# Revit family: ToothbrushHolder-Vitra-EternitySeries-A4487257
name_source: partatom
category: Plumbing Fixtures
revit_build: Autodesk Revit 2017 (Build: 20160225_1515(x64)
units: mm (PartAtom-declared; Revit-internal decimal feet)

## family parameters
Cut with Voids When Loaded = No
Host = Face
OmniClass Number = 23.45.05.14.99
OmniClass Title = Other Sanitary Washing Plumbing Fixtures
Part Type = Normal
Room Calculation Point = No
Round Connector Dimension = Use Diameter
Shared = Yes

## types (8) — shared parameters
BIMobject category = Sanitary - Accessories
CW Connection = No
Depth(mm) = 118 mm
Description = Eternity Toothbrush Holder
Design country = Turkey
HW Connection = No
Height(mm) = 103 mm  [stored 0.337927 ft]
IFC Classification = Sanitary Terminal
Manufacturer = Vitra
Manufacturer name = Vitra
Masterformat 2014 Code = 10 28 16
Masterformat 2014 Description = Bath Accessories
MountingType = Wall-mounted
NBS Referans Code = 35-75-89
NBS Referans Description = Toothbrush Holders
Nominal height = 0.000
Nominal width = 0.000
OmniClass Code = 23-31 25 00
OmniClass Description = Toilet and Bath Specialties
Product Type = Built-in Toothbrush Holder
Product certification = https://vitraglobal.com
Product data url = https://www.vitraglobal.com
Product family = EternitySeries
Product group = Toothbrush Holder
Technical description = https://www.vitra.com.tr
UNSPSC Code = 56
UNSPSC Description = Furniture and Furnishings
URL = https://vitraglobal.com
Uniclass 1.4 Code = L824
Uniclass 1.4 Description = Bathroom, toilet furniture and fittings
Uniclass 2.0 Code = PR-35-75-89
Uniclass 2.0 Description = Toothbrush Holders
Uniclass 2015 Code = Pr_40_20_76_89
Uniclass 2015 Name = Toothbrush holders
Uniformat II Code = E1090
Uniformat II Description = Other Equipment
Vent Connection = No
Warranty Period (Year) = 5 Years
Waste Connection = No
Weight Net (kg) = 0,620
Width(mm) = 103 mm  [stored 0.337927 ft]
Youtube = https://www.youtube.com
zero-valued in all types: CWFU, Cost, Default Elevation, HWFU, WFU

## per-type parameters (varying)
| type | Article No. (default) | Coating Material | Color | Model | Product SKU | Second Material |
| ToothBrushHolder-Vitra-EternitySeries(White)- A4487257 | A4487257 | White | White | A4487257 | A4487257 | Chrome |
| ToothBrushHolder-Vitra-EternitySeries(White)- A4487257EXP | A4487257EXP | White | White | A4487257EXP | A4487257EXP | Chrome |
| ToothBrushHolder-Vitra-EternitySeries(Black)- A4487258 | A4487258 | Black | Black | A4487258 | A4487258 | Chrome |
| ToothBrushHolder-Vitra-EternitySeries(Black)- A4487258EXP | A4487258EXP | Black | Black | A4487258EXP | A4487258EXP | Chrome |
| ToothBrushHolder-Vitra-EternitySeries(Black)- A4487264 | A4487264 | Black | Black | A4487264 | A4487264 | Gold |
| ToothBrushHolder-Vitra-EternitySeries(Black)- A4487264EXP | A4487264EXP | Black | Black | A4487264EXP | A4487264EXP | Gold |
| ToothBrushHolder-Vitra-EternitySeries(White)- A4487227 | A4487227 | White | White | A4487227 | A4487227 | Copper |
| ToothBrushHolder-Vitra-EternitySeries(Black)- A4487228 | A4487228 | Black | Black | A4487228 | A4487228 | Copper |

note: [stored X ft] marks values corroborated as IEEE doubles in the binary element streams (Revit-internal decimal feet)

## geometry (parser evidence)
native form markers: Sweep x3
no freeform markers — native parametric forms only
